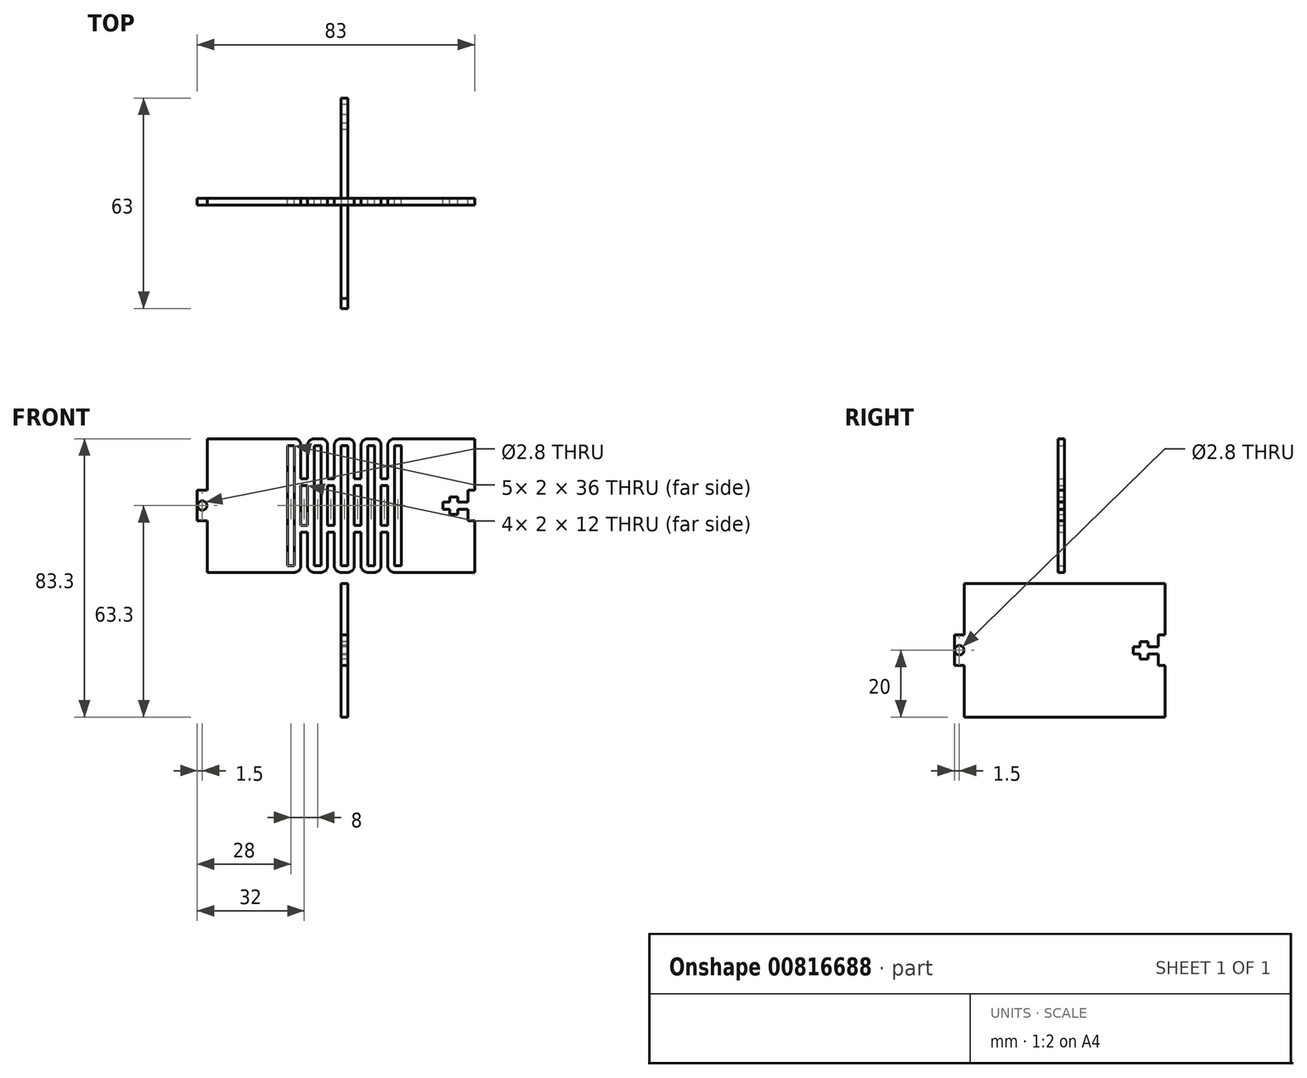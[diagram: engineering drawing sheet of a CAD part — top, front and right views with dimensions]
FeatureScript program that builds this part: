
annotation { "Feature Type Name" : "Feature", "Feature Type Description" : "" }
export const myFeature = defineFeature(function(context is Context, id is Id, definition is map)
    precondition{}
    {
        {
            var Q0;
            Q0=qCreatedBy(makeId("Front.planeOp"),FACE);
            var sketch = newSketch(context, id + "F0", { "sketchPlane" : qUnion([Q0])});
            skLineSegment(sketch, "E0.bottom", {"start": v(-40, 63.3) * mm, "end": v(40, 63.3) * mm});
            skLineSegment(sketch, "E0.top", {"start": v(-40, 23.3) * mm, "end": v(40, 23.3) * mm});
            skLineSegment(sketch, "E0.left", {"start": v(-40, 63.3) * mm, "end": v(-40, 23.3) * mm});
            skLineSegment(sketch, "E0.right", {"start": v(40, 63.3) * mm, "end": v(40, 23.3) * mm});
            skLineSegment(sketch, "E1.bottom", {"start": v(-16, 61.3) * mm, "end": v(-14, 61.3) * mm});
            skLineSegment(sketch, "E1.top", {"start": v(-16, 25.3) * mm, "end": v(-14, 25.3) * mm});
            skLineSegment(sketch, "E1.left", {"start": v(-16, 61.3) * mm, "end": v(-16, 25.3) * mm});
            skLineSegment(sketch, "E1.right", {"start": v(-14, 61.3) * mm, "end": v(-14, 25.3) * mm});
            skLineSegment(sketch, "E2.1.0.0", {"start": v(-6, 61.3) * mm, "end": v(-6, 25.3) * mm});
            skLineSegment(sketch, "E2.1.0.1", {"start": v(-8, 61.3) * mm, "end": v(-8, 25.3) * mm});
            skLineSegment(sketch, "E2.1.0.2", {"start": v(-8, 61.3) * mm, "end": v(-6, 61.3) * mm});
            skLineSegment(sketch, "E2.1.0.3", {"start": v(-8, 25.3) * mm, "end": v(-6, 25.3) * mm});
            skLineSegment(sketch, "E2.2.0.0", {"start": v(2, 61.3) * mm, "end": v(2, 25.3) * mm});
            skLineSegment(sketch, "E2.2.0.1", {"start": v(0, 61.3) * mm, "end": v(0, 25.3) * mm});
            skLineSegment(sketch, "E2.2.0.2", {"start": v(0, 61.3) * mm, "end": v(2, 61.3) * mm});
            skLineSegment(sketch, "E2.2.0.3", {"start": v(0, 25.3) * mm, "end": v(2, 25.3) * mm});
            skLineSegment(sketch, "E2.3.0.0", {"start": v(10, 61.3) * mm, "end": v(10, 25.3) * mm});
            skLineSegment(sketch, "E2.3.0.1", {"start": v(8, 61.3) * mm, "end": v(8, 25.3) * mm});
            skLineSegment(sketch, "E2.3.0.2", {"start": v(8, 61.3) * mm, "end": v(10, 61.3) * mm});
            skLineSegment(sketch, "E2.3.0.3", {"start": v(8, 25.3) * mm, "end": v(10, 25.3) * mm});
            skLineSegment(sketch, "E2.4.0.0", {"start": v(18, 61.3) * mm, "end": v(18, 25.3) * mm});
            skLineSegment(sketch, "E2.4.0.1", {"start": v(16, 61.3) * mm, "end": v(16, 25.3) * mm});
            skLineSegment(sketch, "E2.4.0.2", {"start": v(16, 61.3) * mm, "end": v(18, 61.3) * mm});
            skLineSegment(sketch, "E2.4.0.3", {"start": v(16, 25.3) * mm, "end": v(18, 25.3) * mm});
            skLineSegment(sketch, "E2.direction1", {"start": v(-16, 25.3) * mm, "end": v(-8, 25.3) * mm, "construction": true});
            skLineSegment(sketch, "E3.bottom", {"start": v(-12, 63.3) * mm, "end": v(-10, 63.3) * mm});
            skLineSegment(sketch, "E3.top", {"start": v(-12, 51.3) * mm, "end": v(-10, 51.3) * mm});
            skLineSegment(sketch, "E3.left", {"start": v(-12, 63.3) * mm, "end": v(-12, 51.3) * mm});
            skLineSegment(sketch, "E3.right", {"start": v(-10, 63.3) * mm, "end": v(-10, 51.3) * mm});
            skLineSegment(sketch, "E4.bottom", {"start": v(-12, 49.3) * mm, "end": v(-10, 49.3) * mm});
            skLineSegment(sketch, "E4.top", {"start": v(-12, 37.3) * mm, "end": v(-10, 37.3) * mm});
            skLineSegment(sketch, "E4.left", {"start": v(-12, 49.3) * mm, "end": v(-12, 37.3) * mm});
            skLineSegment(sketch, "E4.right", {"start": v(-10, 49.3) * mm, "end": v(-10, 37.3) * mm});
            skLineSegment(sketch, "E5.bottom", {"start": v(-12, 35.3) * mm, "end": v(-10, 35.3) * mm});
            skLineSegment(sketch, "E5.top", {"start": v(-12, 23.3) * mm, "end": v(-10, 23.3) * mm});
            skLineSegment(sketch, "E5.left", {"start": v(-12, 35.3) * mm, "end": v(-12, 23.3) * mm});
            skLineSegment(sketch, "E5.right", {"start": v(-10, 35.3) * mm, "end": v(-10, 23.3) * mm});
            skLineSegment(sketch, "E6.1.0.0", {"start": v(-4, 63.3) * mm, "end": v(-4, 51.3) * mm});
            skLineSegment(sketch, "E6.1.0.1", {"start": v(-2, 63.3) * mm, "end": v(-2, 51.3) * mm});
            skLineSegment(sketch, "E6.1.0.2", {"start": v(-4, 51.3) * mm, "end": v(-2, 51.3) * mm});
            skLineSegment(sketch, "E6.1.0.3", {"start": v(-4, 49.3) * mm, "end": v(-2, 49.3) * mm});
            skLineSegment(sketch, "E6.1.0.4", {"start": v(-4, 49.3) * mm, "end": v(-4, 37.3) * mm});
            skLineSegment(sketch, "E6.1.0.5", {"start": v(-2, 49.3) * mm, "end": v(-2, 37.3) * mm});
            skLineSegment(sketch, "E6.1.0.6", {"start": v(-4, 37.3) * mm, "end": v(-2, 37.3) * mm});
            skLineSegment(sketch, "E6.1.0.7", {"start": v(-4, 35.3) * mm, "end": v(-2, 35.3) * mm});
            skLineSegment(sketch, "E6.1.0.8", {"start": v(-4, 35.3) * mm, "end": v(-4, 23.3) * mm});
            skLineSegment(sketch, "E6.1.0.9", {"start": v(-2, 35.3) * mm, "end": v(-2, 23.3) * mm});
            skLineSegment(sketch, "E6.1.0.10", {"start": v(-4, 23.3) * mm, "end": v(-2, 23.3) * mm});
            skLineSegment(sketch, "E6.1.0.11", {"start": v(-4, 63.3) * mm, "end": v(-2, 63.3) * mm});
            skLineSegment(sketch, "E6.2.0.0", {"start": v(4, 63.3) * mm, "end": v(4, 51.3) * mm});
            skLineSegment(sketch, "E6.2.0.1", {"start": v(6, 63.3) * mm, "end": v(6, 51.3) * mm});
            skLineSegment(sketch, "E6.2.0.2", {"start": v(4, 51.3) * mm, "end": v(6, 51.3) * mm});
            skLineSegment(sketch, "E6.2.0.3", {"start": v(4, 49.3) * mm, "end": v(6, 49.3) * mm});
            skLineSegment(sketch, "E6.2.0.4", {"start": v(4, 49.3) * mm, "end": v(4, 37.3) * mm});
            skLineSegment(sketch, "E6.2.0.5", {"start": v(6, 49.3) * mm, "end": v(6, 37.3) * mm});
            skLineSegment(sketch, "E6.2.0.6", {"start": v(4, 37.3) * mm, "end": v(6, 37.3) * mm});
            skLineSegment(sketch, "E6.2.0.7", {"start": v(4, 35.3) * mm, "end": v(6, 35.3) * mm});
            skLineSegment(sketch, "E6.2.0.8", {"start": v(4, 35.3) * mm, "end": v(4, 23.3) * mm});
            skLineSegment(sketch, "E6.2.0.9", {"start": v(6, 35.3) * mm, "end": v(6, 23.3) * mm});
            skLineSegment(sketch, "E6.2.0.10", {"start": v(4, 23.3) * mm, "end": v(6, 23.3) * mm});
            skLineSegment(sketch, "E6.2.0.11", {"start": v(4, 63.3) * mm, "end": v(6, 63.3) * mm});
            skLineSegment(sketch, "E6.3.0.0", {"start": v(12, 63.3) * mm, "end": v(12, 51.3) * mm});
            skLineSegment(sketch, "E6.3.0.1", {"start": v(14, 63.3) * mm, "end": v(14, 51.3) * mm});
            skLineSegment(sketch, "E6.3.0.2", {"start": v(12, 51.3) * mm, "end": v(14, 51.3) * mm});
            skLineSegment(sketch, "E6.3.0.3", {"start": v(12, 49.3) * mm, "end": v(14, 49.3) * mm});
            skLineSegment(sketch, "E6.3.0.4", {"start": v(12, 49.3) * mm, "end": v(12, 37.3) * mm});
            skLineSegment(sketch, "E6.3.0.5", {"start": v(14, 49.3) * mm, "end": v(14, 37.3) * mm});
            skLineSegment(sketch, "E6.3.0.6", {"start": v(12, 37.3) * mm, "end": v(14, 37.3) * mm});
            skLineSegment(sketch, "E6.3.0.7", {"start": v(12, 35.3) * mm, "end": v(14, 35.3) * mm});
            skLineSegment(sketch, "E6.3.0.8", {"start": v(12, 35.3) * mm, "end": v(12, 23.3) * mm});
            skLineSegment(sketch, "E6.3.0.9", {"start": v(14, 35.3) * mm, "end": v(14, 23.3) * mm});
            skLineSegment(sketch, "E6.3.0.10", {"start": v(12, 23.3) * mm, "end": v(14, 23.3) * mm});
            skLineSegment(sketch, "E6.3.0.11", {"start": v(12, 63.3) * mm, "end": v(14, 63.3) * mm});
            skLineSegment(sketch, "E6.direction1", {"start": v(-12, 23.3) * mm, "end": v(-4, 23.3) * mm, "construction": true});
            skLineSegment(sketch, "E7", {"start": v(-40, 47.9) * mm, "end": v(-43, 47.9) * mm});
            skLineSegment(sketch, "E8", {"start": v(-43, 47.9) * mm, "end": v(-43, 38.7) * mm});
            skLineSegment(sketch, "E9", {"start": v(-43, 38.7) * mm, "end": v(-40, 38.7) * mm});
            skLineSegment(sketch, "E10", {"start": v(40, 47.9) * mm, "end": v(38, 47.9) * mm});
            skLineSegment(sketch, "E11", {"start": v(38, 47.9) * mm, "end": v(38, 44.4) * mm});
            skLineSegment(sketch, "E12", {"start": v(38, 44.4) * mm, "end": v(35, 44.4) * mm});
            skLineSegment(sketch, "E13", {"start": v(35, 44.4) * mm, "end": v(35, 45.9) * mm});
            skLineSegment(sketch, "E14", {"start": v(35, 45.9) * mm, "end": v(32.5, 45.9) * mm});
            skLineSegment(sketch, "E15", {"start": v(32.5, 45.9) * mm, "end": v(32.5, 44.4) * mm});
            skLineSegment(sketch, "E16", {"start": v(32.5, 44.4) * mm, "end": v(30.5, 44.4) * mm});
            skLineSegment(sketch, "E17", {"start": v(30.5, 44.4) * mm, "end": v(30.5, 43.3) * mm});
            skLineSegment(sketch, "E18", {"start": v(-40, 44.8) * mm, "end": v(-40, 41.8) * mm});
            skLineSegment(sketch, "E19", {"start": v(30.5, 43.3) * mm, "end": v(40, 43.3) * mm});
            skLineSegment(sketch, "E20.MirrorCS", {"start": v(30.5, 42.2) * mm, "end": v(30.5, 43.3) * mm});
            skLineSegment(sketch, "E21.MirrorCS", {"start": v(32.5, 42.2) * mm, "end": v(30.5, 42.2) * mm});
            skLineSegment(sketch, "E22.MirrorCS", {"start": v(32.5, 40.7) * mm, "end": v(32.5, 42.2) * mm});
            skLineSegment(sketch, "E23.MirrorCS", {"start": v(35, 40.7) * mm, "end": v(32.5, 40.7) * mm});
            skLineSegment(sketch, "E24.MirrorCS", {"start": v(35, 42.2) * mm, "end": v(35, 40.7) * mm});
            skLineSegment(sketch, "E25.MirrorCS", {"start": v(38, 42.2) * mm, "end": v(35, 42.2) * mm});
            skLineSegment(sketch, "E26.MirrorCS", {"start": v(38, 38.7) * mm, "end": v(38, 42.2) * mm});
            skLineSegment(sketch, "E27.MirrorCS", {"start": v(40, 38.7) * mm, "end": v(38, 38.7) * mm});
            skCircle(sketch, "E28", {"center": v(-41.5, 43.3) * mm, "radius": 1.4 * mm});
            skPoint(sketch, "E28.centerSnap0", {"position": v(-40, 43.3) * mm});
            skSolve(sketch);
        }
        {
            var Q0;
            {var subQ18=sQuery(id+"F0.wireOp",EDGE,"E0.left");Q0=makeQuery(id+"F0.imprint","IMPRINT",FACE,{"disambiguationData":[TD([[makeQuery(id+"F0.imprint","IMPRINT",EDGE,{"derivedFrom":subQ18}),1.0]])]});}
            extrude(context, id + "F1", {"entities" : qUnion([Q0]), "depth" : 2 * mm, "offsetDistance" : 25 * mm});
        }
        {
            var Q0;
            Q0=qCreatedBy(makeId("Right.planeOp"),FACE);
            var sketch = newSketch(context, id + "F2", { "sketchPlane" : qUnion([Q0])});
            skLineSegment(sketch, "E29.bottom", {"start": v(30, -20) * mm, "end": v(-30, -20) * mm});
            skLineSegment(sketch, "E29.top", {"start": v(30, 20) * mm, "end": v(-30, 20) * mm});
            skLineSegment(sketch, "E29.left", {"start": v(30, -20) * mm, "end": v(30, 20) * mm});
            skLineSegment(sketch, "E29.right", {"start": v(-30, -20) * mm, "end": v(-30, 20) * mm});
            skPoint(sketch, "E29.middle", {"position": v(0, 0) * mm});
            skLineSegment(sketch, "E30", {"start": v(30, 4.6) * mm, "end": v(28, 4.6) * mm});
            skLineSegment(sketch, "E31", {"start": v(28, 4.6) * mm, "end": v(28, 1.1) * mm});
            skLineSegment(sketch, "E32", {"start": v(28, 1.1) * mm, "end": v(25, 1.1) * mm});
            skLineSegment(sketch, "E33", {"start": v(25, 1.1) * mm, "end": v(25, 2.6) * mm});
            skLineSegment(sketch, "E34", {"start": v(25, 2.6) * mm, "end": v(22.5, 2.6) * mm});
            skLineSegment(sketch, "E35", {"start": v(22.5, 2.6) * mm, "end": v(22.5, 1.1) * mm});
            skLineSegment(sketch, "E36", {"start": v(22.5, 1.1) * mm, "end": v(20.5, 1.1) * mm});
            skLineSegment(sketch, "E37.MirrorCS", {"start": v(22.5, -1.1) * mm, "end": v(20.5, -1.1) * mm});
            skLineSegment(sketch, "E38.MirrorCS", {"start": v(22.5, -2.6) * mm, "end": v(22.5, -1.1) * mm});
            skLineSegment(sketch, "E39.MirrorCS", {"start": v(25, -2.6) * mm, "end": v(22.5, -2.6) * mm});
            skLineSegment(sketch, "E40.MirrorCS", {"start": v(25, -1.1) * mm, "end": v(25, -2.6) * mm});
            skLineSegment(sketch, "E41.MirrorCS", {"start": v(28, -1.1) * mm, "end": v(25, -1.1) * mm});
            skLineSegment(sketch, "E42.MirrorCS", {"start": v(28, -4.6) * mm, "end": v(28, -1.1) * mm});
            skLineSegment(sketch, "E43.MirrorCS", {"start": v(30, -4.6) * mm, "end": v(28, -4.6) * mm});
            skLineSegment(sketch, "E44", {"start": v(20.5, 1.1) * mm, "end": v(20.5, -1.1) * mm});
            skLineSegment(sketch, "E45", {"start": v(-30, 4.6) * mm, "end": v(-33, 4.6) * mm});
            skLineSegment(sketch, "E46", {"start": v(-33, 4.6) * mm, "end": v(-33, -4.6) * mm});
            skLineSegment(sketch, "E47", {"start": v(-33, -4.6) * mm, "end": v(-30, -4.6) * mm});
            skCircle(sketch, "E48", {"center": v(-31.5, 0) * mm, "radius": 1.4 * mm});
            skPoint(sketch, "E48.centerSnap0", {"position": v(-30, 0) * mm});
            skSolve(sketch);
        }
        {
            var Q0;
            {var subQ5=sQuery(id+"F2.wireOp",EDGE,"E29.bottom");Q0=makeQuery(id+"F2.imprint","IMPRINT",FACE,{"disambiguationData":[TD([[makeQuery(id+"F2.imprint","IMPRINT",EDGE,{"derivedFrom":subQ5}),-1.0]])]});}
            var Q1;
            {var subQ0=sQuery(id+"F2.wireOp",EDGE,"E45");Q1=makeQuery(id+"F2.imprint","IMPRINT",FACE,{"disambiguationData":[TD([[makeQuery(id+"F2.imprint","IMPRINT",EDGE,{"derivedFrom":subQ0}),1.0]])]});}
            var Q2;
            {var subQ0=sQuery(id+"F2.wireOp",EDGE,"E47");Q2=makeQuery(id+"F2.imprint","IMPRINT",FACE,{"disambiguationData":[TD([[makeQuery(id+"F2.imprint","IMPRINT",EDGE,{"derivedFrom":subQ0}),1.0]])]});}
            extrude(context, id + "F3", {"entities" : qUnion([Q0, Q1, Q2]), "operationType" : NewBodyOperationType.ADD, "depth" : 2 * mm, "offsetDistance" : 25 * mm});
        }
        {
            var Q0;
            {var subQ0=sQuery(id+"F0.wireOp",EDGE,"E7");Q0=makeQuery(id+"F0.imprint","IMPRINT",FACE,{"disambiguationData":[TD([[makeQuery(id+"F0.imprint","IMPRINT",EDGE,{"derivedFrom":subQ0}),1.0]])]});}
            var Q1;
            {var subQ0=sQuery(id+"F0.wireOp",EDGE,"E9");Q1=makeQuery(id+"F0.imprint","IMPRINT",FACE,{"disambiguationData":[TD([[makeQuery(id+"F0.imprint","IMPRINT",EDGE,{"derivedFrom":subQ0}),1.0]])]});}
            extrude(context, id + "F4", {"entities" : qUnion([Q0, Q1]), "operationType" : NewBodyOperationType.ADD, "depth" : 2 * mm, "offsetDistance" : 25 * mm});
        }
        {
            var Q0;
            Q0=makeQuery(id+"F1.opExtrude","SWEPT_EDGE",EDGE,{"disambiguationData":[OSD([sQuery(id+"F0.wireOp",EDGE,"E0.top"),sQuery(id+"F0.wireOp",EDGE,"E5.top"),sQuery(id+"F0.wireOp",EDGE,"E5.right")])]});
            var Q1;
            Q1=makeQuery(id+"F1.opExtrude","SWEPT_EDGE",EDGE,{"disambiguationData":[OSD([sQuery(id+"F0.wireOp",EDGE,"E0.top"),sQuery(id+"F0.wireOp",EDGE,"E6.1.0.8"),sQuery(id+"F0.wireOp",EDGE,"E6.1.0.10")])]});
            var Q2;
            Q2=makeQuery(id+"F1.opExtrude","SWEPT_EDGE",EDGE,{"disambiguationData":[OSD([sQuery(id+"F0.wireOp",EDGE,"E0.top"),sQuery(id+"F0.wireOp",EDGE,"E6.1.0.9"),sQuery(id+"F0.wireOp",EDGE,"E6.1.0.10")])]});
            var Q3;
            Q3=makeQuery(id+"F1.opExtrude","SWEPT_EDGE",EDGE,{"disambiguationData":[OSD([sQuery(id+"F0.wireOp",EDGE,"E0.top"),sQuery(id+"F0.wireOp",EDGE,"E6.2.0.8"),sQuery(id+"F0.wireOp",EDGE,"E6.2.0.10")])]});
            var Q4;
            Q4=makeQuery(id+"F1.opExtrude","SWEPT_EDGE",EDGE,{"disambiguationData":[OSD([sQuery(id+"F0.wireOp",EDGE,"E0.top"),sQuery(id+"F0.wireOp",EDGE,"E6.2.0.9"),sQuery(id+"F0.wireOp",EDGE,"E6.2.0.10")])]});
            var Q5;
            Q5=makeQuery(id+"F1.opExtrude","SWEPT_EDGE",EDGE,{"disambiguationData":[OSD([sQuery(id+"F0.wireOp",EDGE,"E0.top"),sQuery(id+"F0.wireOp",EDGE,"E6.3.0.8"),sQuery(id+"F0.wireOp",EDGE,"E6.3.0.10")])]});
            var Q6;
            Q6=makeQuery(id+"F1.opExtrude","SWEPT_EDGE",EDGE,{"disambiguationData":[OSD([sQuery(id+"F0.wireOp",EDGE,"E0.top"),sQuery(id+"F0.wireOp",EDGE,"E6.3.0.9"),sQuery(id+"F0.wireOp",EDGE,"E6.3.0.10")])]});
            var Q7;
            Q7=makeQuery(id+"F1.opExtrude","SWEPT_EDGE",EDGE,{"disambiguationData":[OSD([sQuery(id+"F0.wireOp",EDGE,"E0.top"),sQuery(id+"F0.wireOp",EDGE,"E5.top"),sQuery(id+"F0.wireOp",EDGE,"E5.left")])]});
            var Q8;
            Q8=makeQuery(id+"F1.opExtrude","SWEPT_EDGE",EDGE,{"disambiguationData":[OSD([sQuery(id+"F0.wireOp",EDGE,"E0.bottom"),sQuery(id+"F0.wireOp",EDGE,"E3.bottom"),sQuery(id+"F0.wireOp",EDGE,"E3.left")])]});
            var Q9;
            Q9=makeQuery(id+"F1.opExtrude","SWEPT_EDGE",EDGE,{"disambiguationData":[OSD([sQuery(id+"F0.wireOp",EDGE,"E0.bottom"),sQuery(id+"F0.wireOp",EDGE,"E3.bottom"),sQuery(id+"F0.wireOp",EDGE,"E3.right")])]});
            var Q10;
            Q10=makeQuery(id+"F1.opExtrude","SWEPT_EDGE",EDGE,{"disambiguationData":[OSD([sQuery(id+"F0.wireOp",EDGE,"E0.bottom"),sQuery(id+"F0.wireOp",EDGE,"E6.1.0.0"),sQuery(id+"F0.wireOp",EDGE,"E6.1.0.11")])]});
            var Q11;
            Q11=makeQuery(id+"F1.opExtrude","SWEPT_EDGE",EDGE,{"disambiguationData":[OSD([sQuery(id+"F0.wireOp",EDGE,"E0.bottom"),sQuery(id+"F0.wireOp",EDGE,"E6.1.0.1"),sQuery(id+"F0.wireOp",EDGE,"E6.1.0.11")])]});
            var Q12;
            Q12=makeQuery(id+"F1.opExtrude","SWEPT_EDGE",EDGE,{"disambiguationData":[OSD([sQuery(id+"F0.wireOp",EDGE,"E0.bottom"),sQuery(id+"F0.wireOp",EDGE,"E6.2.0.0"),sQuery(id+"F0.wireOp",EDGE,"E6.2.0.11")])]});
            var Q13;
            Q13=makeQuery(id+"F1.opExtrude","SWEPT_EDGE",EDGE,{"disambiguationData":[OSD([sQuery(id+"F0.wireOp",EDGE,"E0.bottom"),sQuery(id+"F0.wireOp",EDGE,"E6.2.0.1"),sQuery(id+"F0.wireOp",EDGE,"E6.2.0.11")])]});
            var Q14;
            Q14=makeQuery(id+"F1.opExtrude","SWEPT_EDGE",EDGE,{"disambiguationData":[OSD([sQuery(id+"F0.wireOp",EDGE,"E0.bottom"),sQuery(id+"F0.wireOp",EDGE,"E6.3.0.0"),sQuery(id+"F0.wireOp",EDGE,"E6.3.0.11")])]});
            var Q15;
            Q15=makeQuery(id+"F1.opExtrude","SWEPT_EDGE",EDGE,{"disambiguationData":[OSD([sQuery(id+"F0.wireOp",EDGE,"E0.bottom"),sQuery(id+"F0.wireOp",EDGE,"E6.3.0.1"),sQuery(id+"F0.wireOp",EDGE,"E6.3.0.11")])]});
            fillet(context, id + "F5", {"entities" : qUnion([Q0, Q1, Q2, Q3, Q4, Q5, Q6, Q7, Q8, Q9, Q10, Q11, Q12, Q13, Q14, Q15]), "radius" : 2 * mm, "tangentPropagation" : true, "allowEdgeOverflow" : false});
        }
    });
